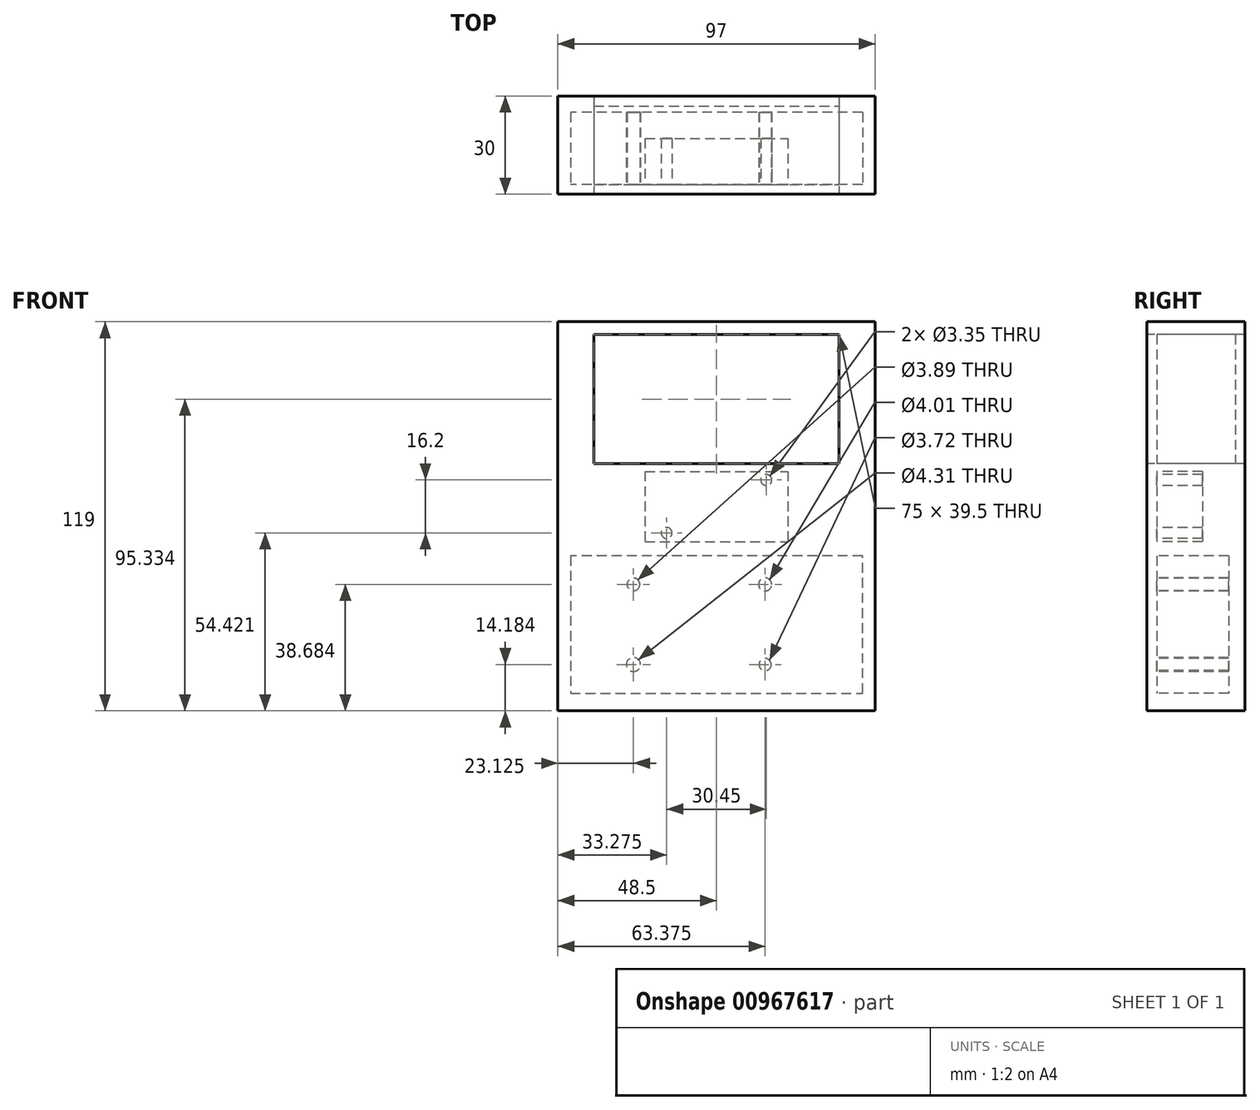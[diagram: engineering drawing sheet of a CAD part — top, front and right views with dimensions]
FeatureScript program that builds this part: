
annotation { "Feature Type Name" : "Feature", "Feature Type Description" : "" }
export const myFeature = defineFeature(function(context is Context, id is Id, definition is map)
    precondition{}
    {
        {
            var Q0;
            Q0=qCreatedBy(makeId("Front.planeOp"),FACE);
            var sketch = newSketch(context, id + "F0", { "sketchPlane" : qUnion([Q0])});
            skPoint(sketch, "E0.middle", {"position": v(0, 0) * mm});
            skLineSegment(sketch, "E1.bottom", {"start": v(-37.5, 47.6) * mm, "end": v(37.5, 47.6) * mm});
            skLineSegment(sketch, "E1.top", {"start": v(-37.5, 8.1) * mm, "end": v(37.5, 8.1) * mm});
            skLineSegment(sketch, "E1.left", {"start": v(-37.5, 47.6) * mm, "end": v(-37.5, 8.1) * mm});
            skLineSegment(sketch, "E1.right", {"start": v(37.5, 47.6) * mm, "end": v(37.5, 8.1) * mm});
            skPoint(sketch, "E2", {"position": v(0, 47.6) * mm});
            skLineSegment(sketch, "E3", {"start": v(0, 47.6) * mm, "end": v(0, 8.1) * mm, "construction": true});
            skPoint(sketch, "E4", {"position": v(0, 27.84) * mm});
            skSolve(sketch);
        }
        {
            var Q0;
            Q0=qCreatedBy(makeId("Front.planeOp"),FACE);
            var sketch = newSketch(context, id + "F1", { "sketchPlane" : qUnion([Q0])});
            skLineSegment(sketch, "E5.0.0", {"start": v(-44.62, -20.06) * mm, "end": v(-44.63, -62.06) * mm});
            skLineSegment(sketch, "E5.0.1", {"start": v(-44.63, -62.06) * mm, "end": v(44.63, -62.06) * mm});
            skLineSegment(sketch, "E5.0.2", {"start": v(44.62, -62.06) * mm, "end": v(44.62, -20.06) * mm});
            skLineSegment(sketch, "E5.0.3", {"start": v(44.63, -20.06) * mm, "end": v(-44.62, -20.06) * mm});
            skLineSegment(sketch, "E6", {"start": v(-25.38, -20.06) * mm, "end": v(-25.38, -62.06) * mm, "construction": true});
            skLineSegment(sketch, "E7", {"start": v(14.87, -20.06) * mm, "end": v(14.87, -62.06) * mm, "construction": true});
            skCircle(sketch, "E8", {"center": v(-25.38, -28.8) * mm, "radius": 1.94 * mm});
            skCircle(sketch, "E9", {"center": v(14.87, -28.8) * mm, "radius": 2 * mm});
            skCircle(sketch, "E10", {"center": v(14.87, -53.3) * mm, "radius": 1.86 * mm});
            skCircle(sketch, "E11", {"center": v(-25.38, -53.3) * mm, "radius": 2.15 * mm});
            skPoint(sketch, "E12", {"position": v(0, -62.06) * mm});
            skPoint(sketch, "E13", {"position": v(0, -20.06) * mm});
            skLineSegment(sketch, "E14", {"start": v(0, -20.06) * mm, "end": v(0, -62.06) * mm, "construction": true});
            skSolve(sketch);
        }
        {
            var Q0;
            Q0=qCreatedBy(makeId("Front.planeOp"),FACE);
            var sketch = newSketch(context, id + "F2", { "sketchPlane" : qUnion([Q0])});
            skLineSegment(sketch, "E15.bottom", {"start": v(-21.88, 5.78) * mm, "end": v(21.88, 5.78) * mm});
            skLineSegment(sketch, "E15.top", {"start": v(-21.88, -15.72) * mm, "end": v(21.88, -15.72) * mm});
            skLineSegment(sketch, "E15.left", {"start": v(-21.88, 5.78) * mm, "end": v(-21.88, -15.72) * mm});
            skLineSegment(sketch, "E15.right", {"start": v(21.88, 5.78) * mm, "end": v(21.88, -15.72) * mm});
            skPoint(sketch, "E16", {"position": v(21.88, -13.07) * mm});
            skPoint(sketch, "E17", {"position": v(-21.88, 3.13) * mm});
            skLineSegment(sketch, "E18", {"start": v(21.88, -13.07) * mm, "end": v(-21.88, -13.07) * mm, "construction": true});
            skPoint(sketch, "E19", {"position": v(15.23, -13.07) * mm});
            skLineSegment(sketch, "E20", {"start": v(-21.88, 3.13) * mm, "end": v(21.88, 3.13) * mm, "construction": true});
            skPoint(sketch, "E21", {"position": v(-15.23, 3.13) * mm});
            skCircle(sketch, "E22", {"center": v(15.23, 3.13) * mm, "radius": 1.68 * mm});
            skCircle(sketch, "E23", {"center": v(-15.23, -13.07) * mm, "radius": 1.68 * mm});
            skPoint(sketch, "E24", {"position": v(0, 5.78) * mm});
            skPoint(sketch, "E25", {"position": v(0, -15.72) * mm});
            skLineSegment(sketch, "E26", {"start": v(0, 5.78) * mm, "end": v(0, -15.72) * mm, "construction": true});
            skSolve(sketch);
        }
        {
            var Q0;
            Q0=qCreatedBy(makeId("Front.planeOp"),FACE);
            var sketch = newSketch(context, id + "F3", { "sketchPlane" : qUnion([Q0])});
            skLineSegment(sketch, "E27.bottom", {"start": v(-48.5, 51.51) * mm, "end": v(48.5, 51.51) * mm});
            skLineSegment(sketch, "E27.top", {"start": v(-48.5, -67.49) * mm, "end": v(48.5, -67.49) * mm});
            skLineSegment(sketch, "E27.left", {"start": v(-48.5, 51.51) * mm, "end": v(-48.5, -67.49) * mm});
            skLineSegment(sketch, "E27.right", {"start": v(48.5, 51.51) * mm, "end": v(48.5, -67.49) * mm});
            skPoint(sketch, "E28", {"position": v(0, 51.51) * mm});
            skLineSegment(sketch, "E29.0.0", {"start": v(-37.5, 47.6) * mm, "end": v(-37.5, 8.1) * mm});
            skLineSegment(sketch, "E29.0.1", {"start": v(-37.5, 8.1) * mm, "end": v(37.5, 8.1) * mm});
            skLineSegment(sketch, "E29.0.2", {"start": v(37.5, 8.1) * mm, "end": v(37.5, 47.6) * mm});
            skLineSegment(sketch, "E29.0.3", {"start": v(37.5, 47.6) * mm, "end": v(-37.5, 47.6) * mm});
            skLineSegment(sketch, "E30.0.0", {"start": v(44.62, -62.06) * mm, "end": v(44.63, -20.06) * mm});
            skLineSegment(sketch, "E30.0.1", {"start": v(44.62, -20.06) * mm, "end": v(-44.62, -20.06) * mm});
            skLineSegment(sketch, "E30.0.2", {"start": v(-44.62, -20.06) * mm, "end": v(-44.62, -62.06) * mm});
            skLineSegment(sketch, "E30.0.3", {"start": v(-44.63, -62.06) * mm, "end": v(44.63, -62.06) * mm});
            skLineSegment(sketch, "E31.0.0", {"start": v(-21.88, 5.78) * mm, "end": v(-21.88, -15.72) * mm});
            skLineSegment(sketch, "E31.0.1", {"start": v(-21.88, -15.72) * mm, "end": v(21.88, -15.72) * mm});
            skLineSegment(sketch, "E31.0.2", {"start": v(21.88, -15.72) * mm, "end": v(21.88, 5.78) * mm});
            skLineSegment(sketch, "E31.0.3", {"start": v(21.88, 5.78) * mm, "end": v(-21.88, 5.78) * mm});
            skSolve(sketch);
        }
        {
            var Q0;
            Q0=makeQuery(id+"F3.imprint","IMPRINT",FACE,{"disambiguationData":[TD([[makeQuery(id+"F3.imprint","IMPRINT",EDGE,{"derivedFrom":sQuery(id+"F3.wireOp",EDGE,"E27.bottom")}),-1.0]])]});
            var Q1;
            Q1=makeQuery(id+"F3.imprint","IMPRINT",FACE,{"disambiguationData":[TD([[makeQuery(id+"F3.imprint","IMPRINT",EDGE,{"derivedFrom":sQuery(id+"F3.wireOp",EDGE,"E29.0.0")}),1.0]])]});
            var Q2;
            Q2=makeQuery(id+"F3.imprint","IMPRINT",FACE,{"disambiguationData":[TD([[makeQuery(id+"F3.imprint","IMPRINT",EDGE,{"derivedFrom":sQuery(id+"F3.wireOp",EDGE,"E31.0.0")}),1.0]])]});
            var Q3;
            Q3=makeQuery(id+"F3.imprint","IMPRINT",FACE,{"disambiguationData":[TD([[makeQuery(id+"F3.imprint","IMPRINT",EDGE,{"derivedFrom":sQuery(id+"F3.wireOp",EDGE,"E30.0.0")}),1.0]])]});
            extrude(context, id + "F4", {"entities" : qUnion([Q0, Q1, Q2, Q3]), "oppositeDirection" : true, "depth" : 27 * mm, "offsetDistance" : 25 * mm, "hasSecondDirection" : true, "secondDirectionOppositeDirection" : false, "secondDirectionDepth" : 3 * mm});
        }
        {
            var Q0;
            Q0=makeQuery(id+"F4.opExtrude","CAP_FACE",FACE,{"disambiguationData":[OSD([sQuery(id+"F3.wireOp",EDGE,"E27.bottom"),sQuery(id+"F3.wireOp",EDGE,"E27.top"),sQuery(id+"F3.wireOp",EDGE,"E27.left"),sQuery(id+"F3.wireOp",EDGE,"E27.right")])],"isStart":true});
            var sketch = newSketch(context, id + "F5", { "sketchPlane" : qUnion([Q0])});
            skLineSegment(sketch, "E32.0", {"start": v(37.5, 47.6) * mm, "end": v(-37.5, 47.6) * mm});
            skLineSegment(sketch, "E32.1", {"start": v(-37.5, 47.6) * mm, "end": v(-37.5, 8.1) * mm});
            skLineSegment(sketch, "E32.2", {"start": v(-37.5, 8.1) * mm, "end": v(37.5, 8.1) * mm});
            skLineSegment(sketch, "E32.3", {"start": v(37.5, 8.1) * mm, "end": v(37.5, 47.6) * mm});
            skSolve(sketch);
        }
        {
            var Q0;
            Q0 = qSketchRegion(id + "F5", true);
            extrude(context, id + "F6", {"entities" : qUnion([Q0]), "operationType" : NewBodyOperationType.REMOVE, "endBound" : BoundingType.UP_TO_NEXT, "oppositeDirection" : true, "depth" : 25 * mm, "offsetDistance" : 25 * mm});
        }
        {
            var Q0;
            Q0=makeQuery(id+"F0.imprint","IMPRINT",FACE,{"disambiguationData":[TD([[makeQuery(id+"F0.imprint","IMPRINT",EDGE,{"derivedFrom":sQuery(id+"F0.wireOp",EDGE,"E1.bottom")}),-1.0]])]});
            extrude(context, id + "F7", {"entities" : qUnion([Q0]), "oppositeDirection" : true, "depth" : 24 * mm, "offsetDistance" : 25 * mm});
        }
        {
            var Q0;
            Q0=makeQuery(id+"F1.imprint","IMPRINT",FACE,{"disambiguationData":[TD([[makeQuery(id+"F1.imprint","IMPRINT",EDGE,{"derivedFrom":sQuery(id+"F1.wireOp",EDGE,"E5.0.0")}),1.0]])]});
            extrude(context, id + "F8", {"entities" : qUnion([Q0]), "oppositeDirection" : true, "depth" : 22 * mm, "offsetDistance" : 25 * mm});
        }
        {
            var Q0;
            Q0=makeQuery(id+"F2.imprint","IMPRINT",FACE,{"disambiguationData":[TD([[makeQuery(id+"F2.imprint","IMPRINT",EDGE,{"derivedFrom":sQuery(id+"F2.wireOp",EDGE,"E15.bottom")}),-1.0]])]});
            extrude(context, id + "F9", {"entities" : qUnion([Q0]), "oppositeDirection" : true, "depth" : 14 * mm, "offsetDistance" : 25 * mm});
        }
    });
